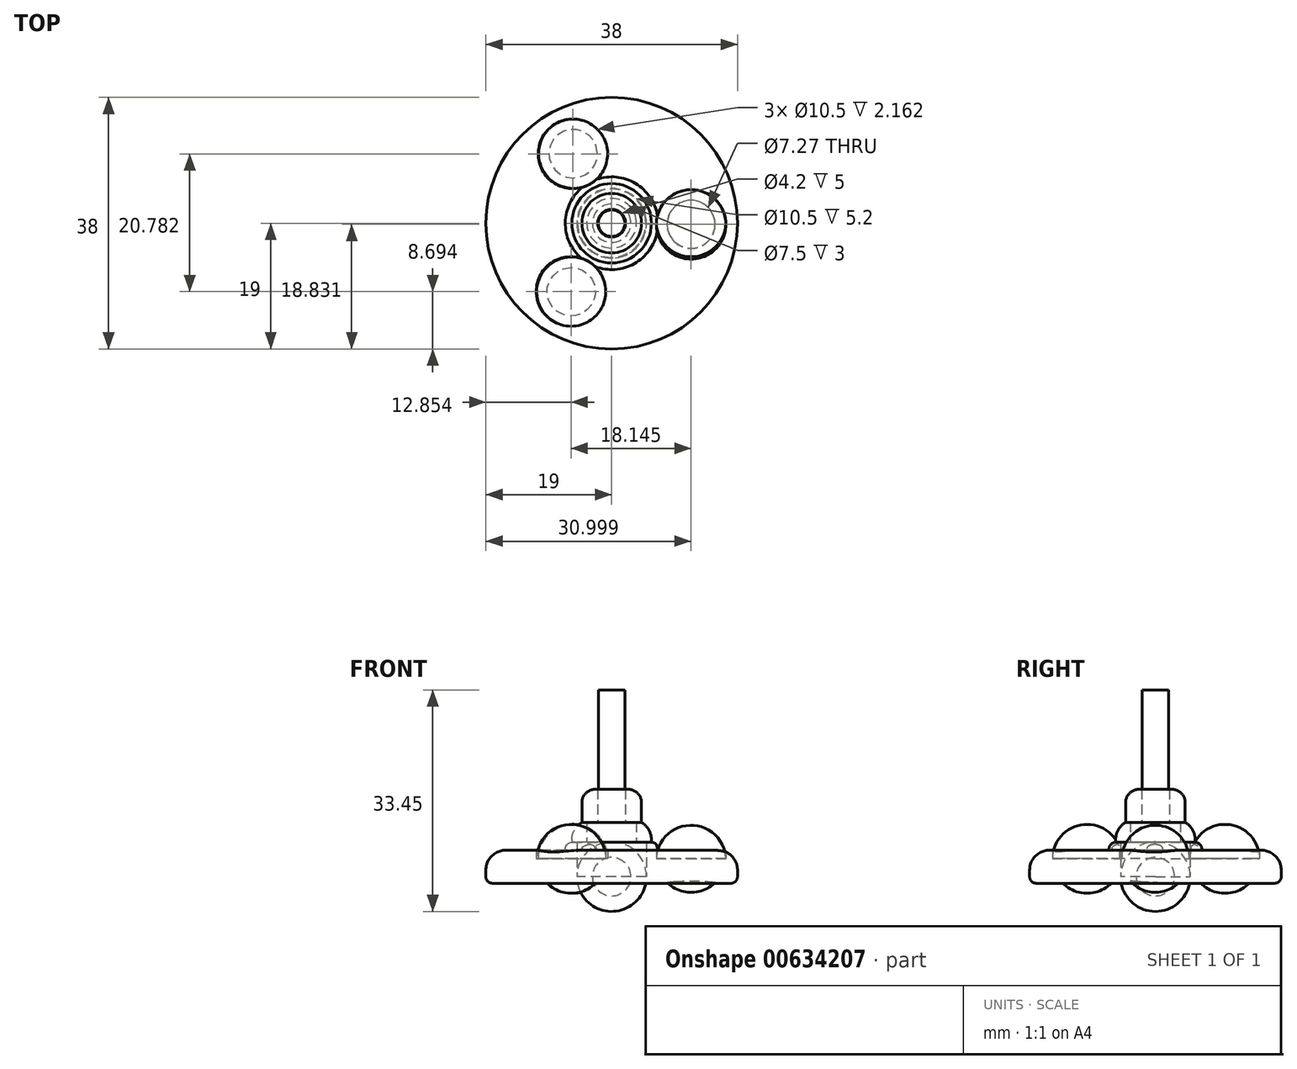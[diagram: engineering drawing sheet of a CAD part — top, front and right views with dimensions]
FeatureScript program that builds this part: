
annotation { "Feature Type Name" : "Feature", "Feature Type Description" : "" }
export const myFeature = defineFeature(function(context is Context, id is Id, definition is map)
    precondition{}
    {
        {
            var Q0;
            Q0=qCreatedBy(makeId("Top.planeOp"),FACE);
            var sketch = newSketch(context, id + "F0", { "sketchPlane" : qUnion([Q0])});
            skCircle(sketch, "E0", {"center": v(0, 0) * mm, "radius": 5.25 * mm});
            skCircle(sketch, "E1", {"center": v(0, 0) * mm, "radius": 19 * mm});
            skCircle(sketch, "E2", {"center": v(0, 0) * mm, "radius": 2.9 * mm});
            skCircle(sketch, "E3", {"center": v(12, -0.17) * mm, "radius": 5.25 * mm});
            skCircle(sketch, "E4.1.0", {"center": v(-5.85, 10.48) * mm, "radius": 5.25 * mm});
            skCircle(sketch, "E4.2.0", {"center": v(-6.15, -10.3) * mm, "radius": 5.25 * mm});
            skCircle(sketch, "E5", {"center": v(12, -0.17) * mm, "radius": 3.64 * mm});
            skCircle(sketch, "E6", {"center": v(-5.85, 10.48) * mm, "radius": 3.42 * mm});
            skCircle(sketch, "E7", {"center": v(-6.15, -10.3) * mm, "radius": 3.4 * mm});
            skSolve(sketch);
        }
        {
            var Q0;
            Q0=makeQuery(id+"F0.imprint","IMPRINT",FACE,{"disambiguationData":[TD([[makeQuery(id+"F0.imprint","IMPRINT",EDGE,{"derivedFrom":sQuery(id+"F0.wireOp",EDGE,"E0")}),-1.0]])]});
            extrude(context, id + "F1", {"entities" : qUnion([Q0]), "depth" : 5 * mm, "offsetDistance" : 25 * mm});
        }
        {
            var Q0;
            Q0=makeQuery(id+"F0.imprint","IMPRINT",FACE,{"disambiguationData":[TD([[makeQuery(id+"F0.imprint","IMPRINT",EDGE,{"derivedFrom":sQuery(id+"F0.wireOp",EDGE,"E0")}),1.0]])]});
            extrude(context, id + "F2", {"entities" : qUnion([Q0]), "operationType" : NewBodyOperationType.ADD, "depth" : 1 * mm, "offsetDistance" : 25 * mm});
        }
        {
            var Q0;
            Q0=makeQuery(id+"F2.opExtrude","CAP_FACE",FACE,{"disambiguationData":[OSD([sQuery(id+"F0.wireOp",EDGE,"E0"),sQuery(id+"F0.wireOp",EDGE,"E2")])],"isStart":false});
            var sketch = newSketch(context, id + "F3", { "sketchPlane" : qUnion([Q0])});
            skLineSegment(sketch, "E8", {"start": v(-5.25, 0) * mm, "end": v(5.25, 0) * mm});
            skArc(sketch, "E9", {"start": v(5.25, 0) * mm, "mid": v(0, 5.25) * mm, "end": v(-5.25, 0) * mm});
            skSolve(sketch);
        }
        {
            var Q0;
            {var subQ0=sQuery(id+"F3.wireOp",EDGE,"E9");Q0=makeQuery(id+"F3.imprint","IMPRINT",FACE,{"disambiguationData":[TD([[makeQuery(id+"F3.imprint","IMPRINT",EDGE,{"derivedFrom":subQ0}),1.0]])]});}
            var Q1;
            Q1=sQuery(id+"F3.wireOp",EDGE,"E8");
            revolve(context, id + "F4", {"operationType" : NewBodyOperationType.ADD, "entities" : qUnion([Q0]), "axis" : qUnion([Q1]), "revolveType" : RevolveType.FULL});
        }
        {
            var Q0;
            Q0=makeQuery(id+"F1.opExtrude","CAP_FACE",FACE,{"disambiguationData":[OSD([sQuery(id+"F0.wireOp",EDGE,"E0"),sQuery(id+"F0.wireOp",EDGE,"E1")])],"isStart":false});
            var sketch = newSketch(context, id + "F5", { "sketchPlane" : qUnion([Q0])});
            skCircle(sketch, "E10", {"center": v(0, 0) * mm, "radius": 7 * mm});
            skSolve(sketch);
        }
        {
            var Q0;
            Q0=makeQuery(id+"F5.imprint","IMPRINT",FACE,{"disambiguationData":[TD([[makeQuery(id+"F5.imprint","IMPRINT",EDGE,{"derivedFrom":sQuery(id+"F5.wireOp",EDGE,"E10")}),1.0]])]});
            extrude(context, id + "F6", {"entities" : qUnion([Q0]), "operationType" : NewBodyOperationType.ADD, "depth" : 1.2 * mm, "offsetDistance" : 25 * mm});
        }
        {
            var Q0;
            Q0=makeQuery(id+"F6.opExtrude","CAP_FACE",FACE,{"disambiguationData":[OSD([sQuery(id+"F0.wireOp",EDGE,"E0"),sQuery(id+"F5.wireOp",EDGE,"E10")])],"isStart":false});
            var sketch = newSketch(context, id + "F7", { "sketchPlane" : qUnion([Q0])});
            skCircle(sketch, "E11", {"center": v(0, 0) * mm, "radius": 3.75 * mm});
            skCircle(sketch, "E12", {"center": v(0, 0) * mm, "radius": 6 * mm});
            skSolve(sketch);
        }
        {
            var Q0;
            Q0 = qSketchRegion(id + "F7", true);
            extrude(context, id + "F8", {"entities" : qUnion([Q0]), "operationType" : NewBodyOperationType.ADD, "depth" : 3 * mm, "offsetDistance" : 25 * mm});
        }
        {
            var Q0;
            Q0=makeQuery(id+"F8.opExtrude","CAP_FACE",FACE,{"disambiguationData":[OSD([sQuery(id+"F7.wireOp",EDGE,"E11"),sQuery(id+"F7.wireOp",EDGE,"E12")])],"isStart":false});
            var sketch = newSketch(context, id + "F9", { "sketchPlane" : qUnion([Q0])});
            skCircle(sketch, "E13", {"center": v(0, 0) * mm, "radius": 2.1 * mm});
            skCircle(sketch, "E14", {"center": v(0, 0) * mm, "radius": 4.5 * mm});
            skSolve(sketch);
        }
        {
            var Q0;
            Q0 = qSketchRegion(id + "F9", true);
            extrude(context, id + "F10", {"entities" : qUnion([Q0]), "operationType" : NewBodyOperationType.ADD, "depth" : 5 * mm, "offsetDistance" : 25 * mm});
        }
        {
            var Q0;
            Q0=makeQuery(id+"F10.opExtrude","CAP_EDGE",EDGE,{"disambiguationData":[OSD([sQuery(id+"F9.wireOp",EDGE,"E14")])],"isStart":false});
            fillet(context, id + "F11", {"entities" : qUnion([Q0]), "radius" : 2 * mm, "tangentPropagation" : true, "allowEdgeOverflow" : false});
        }
        {
            var Q0;
            Q0=makeQuery(id+"F8.opExtrude","CAP_EDGE",EDGE,{"disambiguationData":[OSD([sQuery(id+"F7.wireOp",EDGE,"E12")])],"isStart":false});
            fillet(context, id + "F12", {"entities" : qUnion([Q0]), "radius" : 3 * mm, "tangentPropagation" : true, "allowEdgeOverflow" : false});
        }
        {
            var Q0;
            Q0=makeQuery(id+"F1.opExtrude","CAP_EDGE",EDGE,{"disambiguationData":[OSD([sQuery(id+"F0.wireOp",EDGE,"E1")])],"isStart":false});
            fillet(context, id + "F13", {"entities" : qUnion([Q0]), "radius" : 3 * mm, "tangentPropagation" : true, "allowEdgeOverflow" : false});
        }
        {
            var Q0;
            Q0=makeQuery(id+"F1.opExtrude","CAP_EDGE",EDGE,{"disambiguationData":[OSD([sQuery(id+"F0.wireOp",EDGE,"E1")])],"isStart":true});
            fillet(context, id + "F14", {"entities" : qUnion([Q0]), "radius" : 1 * mm, "tangentPropagation" : true, "allowEdgeOverflow" : false});
        }
        {
            var Q0;
            Q0=makeQuery(id+"F10.opExtrude","CAP_FACE",FACE,{"disambiguationData":[OSD([sQuery(id+"F9.wireOp",EDGE,"E13"),sQuery(id+"F9.wireOp",EDGE,"E14")])],"isStart":false});
            var sketch = newSketch(context, id + "F15", { "sketchPlane" : qUnion([Q0])});
            skCircle(sketch, "E15", {"center": v(0, 0) * mm, "radius": 2 * mm});
            skSolve(sketch);
        }
        {
            var Q0;
            Q0 = qSketchRegion(id + "F15", true);
            extrude(context, id + "F16", {"entities" : qUnion([Q0]), "depth" : 15 * mm, "offsetDistance" : 25 * mm});
        }
        {
            var Q0;
            Q0=makeQuery(id+"F0.imprint","IMPRINT",FACE,{"disambiguationData":[TD([[makeQuery(id+"F0.imprint","IMPRINT",EDGE,{"derivedFrom":sQuery(id+"F0.wireOp",EDGE,"E3")}),1.0]])]});
            extrude(context, id + "F17", {"entities" : qUnion([Q0]), "operationType" : NewBodyOperationType.ADD, "depth" : 3.7 * mm, "offsetDistance" : 25 * mm});
        }
        {
            var Q0;
            Q0=makeQuery(id+"F17.opExtrude","CAP_FACE",FACE,{"disambiguationData":[OSD([sQuery(id+"F0.wireOp",EDGE,"E3"),sQuery(id+"F0.wireOp",EDGE,"E5")])],"isStart":false});
            var sketch = newSketch(context, id + "F18", { "sketchPlane" : qUnion([Q0])});
            skArc(sketch, "E16", {"start": v(17.25, 0) * mm, "mid": v(12, 5.07) * mm, "end": v(6.75, 0) * mm});
            skLineSegment(sketch, "E17", {"start": v(6.75, 0) * mm, "end": v(17.25, 0) * mm});
            skLineSegment(sketch, "E18.1.0", {"start": v(-3.38, 5.85) * mm, "end": v(-8.62, 14.94) * mm});
            skArc(sketch, "E18.1.1", {"start": v(-8.62, 14.94) * mm, "mid": v(-10.39, 7.86) * mm, "end": v(-3.38, 5.85) * mm});
            skLineSegment(sketch, "E18.2.0", {"start": v(-3.38, -5.85) * mm, "end": v(-8.62, -14.94) * mm});
            skArc(sketch, "E18.2.1", {"start": v(-8.62, -14.94) * mm, "mid": v(-1.61, -12.92) * mm, "end": v(-3.38, -5.85) * mm});
            skPoint(sketch, "E18.center", {"position": v(0, 0) * mm});
            skSolve(sketch);
        }
        {
            var Q0;
            {var subQ0=sQuery(id+"F18.wireOp",EDGE,"E17");var subQ1=makeQuery(id+"F17.opExtrude","CAP_EDGE",EDGE,{"disambiguationData":[OSD([sQuery(id+"F0.wireOp",EDGE,"E5")])],"isStart":false});var subQ2=makeQuery(id+"F18.imprint","INTERSECT",VERTEX,{"disambiguationData":[OD(0.0)],"derivedFrom":[subQ1,subQ0]});Q0=makeQuery(id+"F18.imprint","IMPRINT",FACE,{"disambiguationData":[TD([[makeQuery(id+"F18.imprint","IMPRINT",EDGE,{"disambiguationData":[TD([[subQ2,-1.0]])],"derivedFrom":subQ0}),1.0]])]});}
            var Q1;
            {var subQ0=sQuery(id+"F18.wireOp",EDGE,"E16");Q1=makeQuery(id+"F18.imprint","IMPRINT",FACE,{"disambiguationData":[TD([[makeQuery(id+"F18.imprint","IMPRINT",EDGE,{"derivedFrom":subQ0}),1.0]])]});}
            var Q2;
            Q2=sQuery(id+"F18.wireOp",EDGE,"E17");
            revolve(context, id + "F19", {"operationType" : NewBodyOperationType.ADD, "entities" : qUnion([Q0, Q1]), "axis" : qUnion([Q2]), "revolveType" : RevolveType.FULL});
        }
        {
            var Q0;
            Q0=makeQuery(id+"F0.imprint","IMPRINT",FACE,{"disambiguationData":[TD([[makeQuery(id+"F0.imprint","IMPRINT",EDGE,{"derivedFrom":sQuery(id+"F0.wireOp",EDGE,"E4.1.0")}),1.0]])]});
            extrude(context, id + "F20", {"entities" : qUnion([Q0]), "operationType" : NewBodyOperationType.ADD, "depth" : 3.7 * mm, "offsetDistance" : 25 * mm});
        }
        {
            var Q0;
            Q0=makeQuery(id+"F20.opExtrude","CAP_FACE",FACE,{"disambiguationData":[OSD([sQuery(id+"F0.wireOp",EDGE,"E4.1.0"),sQuery(id+"F0.wireOp",EDGE,"E6")])],"isStart":false});
            var sketch = newSketch(context, id + "F21", { "sketchPlane" : qUnion([Q0])});
            skLineSegment(sketch, "E19", {"start": v(-2.82, 6.19) * mm, "end": v(-8.8, 14.82) * mm});
            skArc(sketch, "E20", {"start": v(-2.82, 6.19) * mm, "mid": v(-1.54, 13.47) * mm, "end": v(-8.8, 14.82) * mm});
            skSolve(sketch);
        }
        {
            var Q0;
            {var subQ0=sQuery(id+"F21.wireOp",EDGE,"E19");var subQ1=makeQuery(id+"F20.opExtrude","CAP_EDGE",EDGE,{"disambiguationData":[OSD([sQuery(id+"F0.wireOp",EDGE,"E6")])],"isStart":false});var subQ2=makeQuery(id+"F21.imprint","INTERSECT",VERTEX,{"disambiguationData":[OD(0.0)],"derivedFrom":[subQ1,subQ0]});Q0=makeQuery(id+"F21.imprint","IMPRINT",FACE,{"disambiguationData":[TD([[makeQuery(id+"F21.imprint","IMPRINT",EDGE,{"disambiguationData":[TD([[subQ2,-1.0]])],"derivedFrom":subQ0}),-1.0]])]});}
            var Q1;
            {var subQ0=sQuery(id+"F21.wireOp",EDGE,"E20");Q1=makeQuery(id+"F21.imprint","IMPRINT",FACE,{"disambiguationData":[TD([[makeQuery(id+"F21.imprint","IMPRINT",EDGE,{"derivedFrom":subQ0}),1.0]])]});}
            var Q2;
            Q2=sQuery(id+"F21.wireOp",EDGE,"E19");
            revolve(context, id + "F22", {"operationType" : NewBodyOperationType.ADD, "entities" : qUnion([Q0, Q1]), "axis" : qUnion([Q2]), "revolveType" : RevolveType.FULL});
        }
        {
            var Q0;
            Q0=makeQuery(id+"F0.imprint","IMPRINT",FACE,{"disambiguationData":[TD([[makeQuery(id+"F0.imprint","IMPRINT",EDGE,{"derivedFrom":sQuery(id+"F0.wireOp",EDGE,"E4.2.0")}),1.0]])]});
            extrude(context, id + "F23", {"entities" : qUnion([Q0]), "operationType" : NewBodyOperationType.ADD, "depth" : 3.7 * mm, "offsetDistance" : 25 * mm});
        }
        {
            var Q0;
            Q0=makeQuery(id+"F23.opExtrude","CAP_FACE",FACE,{"disambiguationData":[OSD([sQuery(id+"F0.wireOp",EDGE,"E4.2.0"),sQuery(id+"F0.wireOp",EDGE,"E7")])],"isStart":false});
            var sketch = newSketch(context, id + "F24", { "sketchPlane" : qUnion([Q0])});
            skLineSegment(sketch, "E21", {"start": v(-3.27, -5.92) * mm, "end": v(-8.94, -14.75) * mm});
            skArc(sketch, "E22", {"start": v(-8.94, -14.75) * mm, "mid": v(-1.73, -13.14) * mm, "end": v(-3.27, -5.92) * mm});
            skSolve(sketch);
        }
        {
            var Q0;
            {var subQ0=sQuery(id+"F24.wireOp",EDGE,"E21");var subQ1=makeQuery(id+"F23.opExtrude","CAP_EDGE",EDGE,{"disambiguationData":[OSD([sQuery(id+"F0.wireOp",EDGE,"E7")])],"isStart":false});var subQ2=makeQuery(id+"F24.imprint","INTERSECT",VERTEX,{"disambiguationData":[OD(0.0)],"derivedFrom":[subQ1,subQ0]});Q0=makeQuery(id+"F24.imprint","IMPRINT",FACE,{"disambiguationData":[TD([[makeQuery(id+"F24.imprint","IMPRINT",EDGE,{"disambiguationData":[TD([[subQ2,-1.0]])],"derivedFrom":subQ0}),1.0]])]});}
            var Q1;
            {var subQ0=sQuery(id+"F24.wireOp",EDGE,"E22");Q1=makeQuery(id+"F24.imprint","IMPRINT",FACE,{"disambiguationData":[TD([[makeQuery(id+"F24.imprint","IMPRINT",EDGE,{"derivedFrom":subQ0}),1.0]])]});}
            var Q2;
            Q2=sQuery(id+"F24.wireOp",EDGE,"E21");
            revolve(context, id + "F25", {"operationType" : NewBodyOperationType.ADD, "entities" : qUnion([Q0, Q1]), "axis" : qUnion([Q2]), "revolveType" : RevolveType.FULL});
        }
        {
            var Q0;
            {var subQ0=sQuery(id+"F5.wireOp",EDGE,"E10");Q0=makeQuery(id+"F6.opExtrude","CAP_EDGE",EDGE,{"disambiguationData":[OSD([subQ0]),TDD([makeQuery(id+"F5.imprint","IMPRINT",EDGE,{"disambiguationData":[TD([[makeQuery(id+"F5.imprint","INTERSECT",VERTEX,{"disambiguationData":[OD(1.0)],"derivedFrom":[makeQuery(id+"F1.opExtrude","CAP_EDGE",EDGE,{"disambiguationData":[OSD([sQuery(id+"F0.wireOp",EDGE,"E4.1.0")])],"isStart":false}),subQ0]}),-1.0]])],"derivedFrom":subQ0})])],"isStart":false});}
            fillet(context, id + "F26", {"entities" : qUnion([Q0]), "radius" : 1 * mm, "tangentPropagation" : true, "allowEdgeOverflow" : false});
        }
    });
